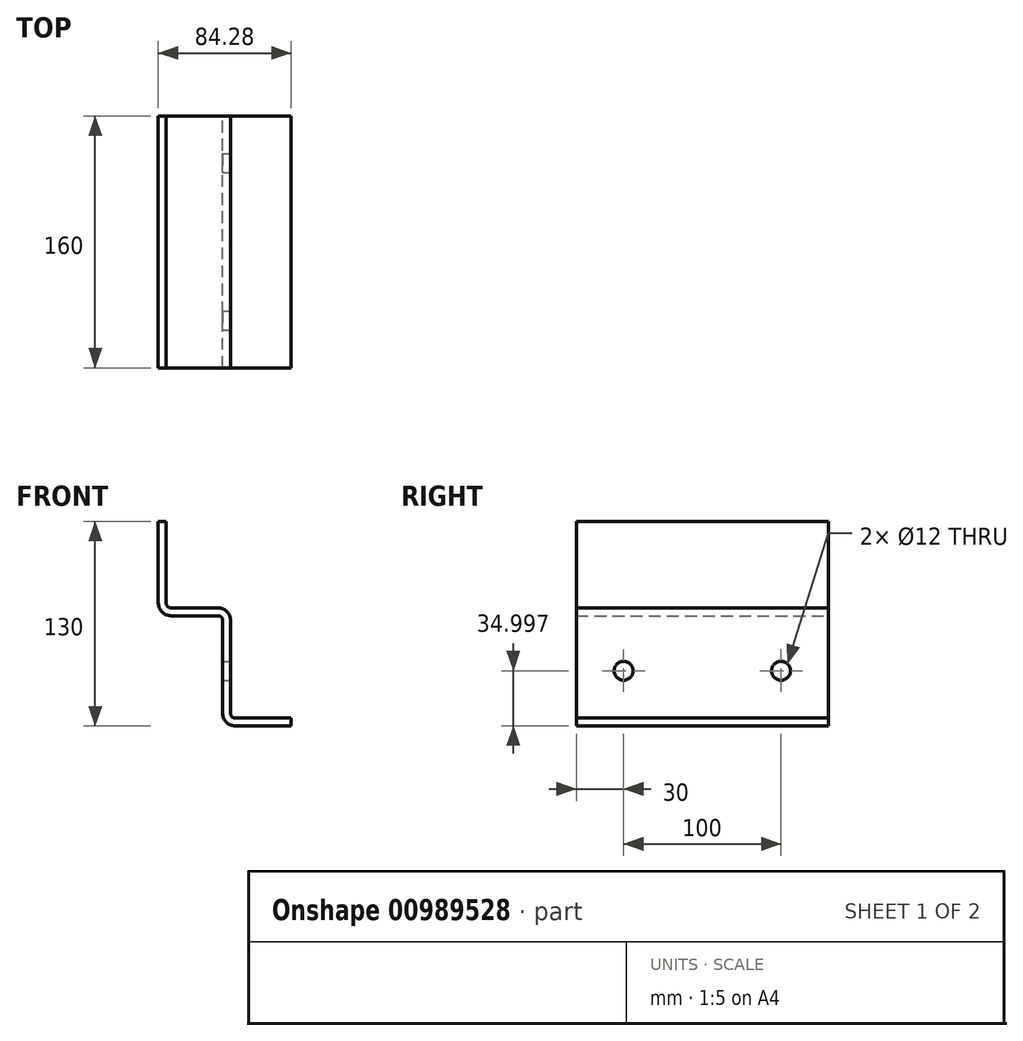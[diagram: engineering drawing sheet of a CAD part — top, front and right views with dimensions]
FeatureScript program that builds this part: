
annotation { "Feature Type Name" : "Feature", "Feature Type Description" : "" }
export const myFeature = defineFeature(function(context is Context, id is Id, definition is map)
    precondition{}
    {
        {
            var Q0;
            Q0=qCreatedBy(makeId("Front.planeOp"),FACE);
            var sketch = newSketch(context, id + "F0", { "sketchPlane" : qUnion([Q0])});
            skLineSegment(sketch, "E0", {"start": v(-40.9, 34.6) * mm, "end": v(-40.9, -17.4) * mm});
            skLineSegment(sketch, "E1", {"start": v(-32.9, -25.4) * mm, "end": v(-3, -25.4) * mm});
            skLineSegment(sketch, "E2", {"start": v(0, -28.4) * mm, "end": v(0, -87.4) * mm});
            skLineSegment(sketch, "E3", {"start": v(8, -95.4) * mm, "end": v(43.4, -95.4) * mm});
            skLineSegment(sketch, "E4", {"start": v(43.4, -95.4) * mm, "end": v(43.4, -90.4) * mm});
            skLineSegment(sketch, "E5", {"start": v(43.4, -90.4) * mm, "end": v(8, -90.4) * mm});
            skLineSegment(sketch, "E6", {"start": v(5, -87.4) * mm, "end": v(5, -28.4) * mm});
            skLineSegment(sketch, "E7", {"start": v(-3, -20.4) * mm, "end": v(-32.9, -20.4) * mm});
            skLineSegment(sketch, "E8", {"start": v(-35.9, -17.4) * mm, "end": v(-35.9, 34.6) * mm});
            skLineSegment(sketch, "E9", {"start": v(-35.9, 34.6) * mm, "end": v(-40.9, 34.6) * mm});
            skArc(sketch, "E10.filletArc", {"start": v(-35.9, -17.4) * mm, "mid": v(-35.01, -19.51) * mm, "end": v(-32.9, -20.4) * mm});
            skPoint(sketch, "E11.visualSharp", {"position": v(0, -25.4) * mm});
            skArc(sketch, "E11.filletArc", {"start": v(0, -28.4) * mm, "mid": v(-0.88, -26.27) * mm, "end": v(-3, -25.4) * mm});
            skPoint(sketch, "E12.visualSharp", {"position": v(5, -90.4) * mm});
            skArc(sketch, "E12.filletArc", {"start": v(5, -87.4) * mm, "mid": v(5.88, -89.51) * mm, "end": v(8, -90.4) * mm});
            skPoint(sketch, "E13.visualSharp", {"position": v(-40.9, -25.4) * mm});
            skArc(sketch, "E13.filletArc", {"start": v(-40.9, -17.4) * mm, "mid": v(-38.55, -23.05) * mm, "end": v(-32.9, -25.4) * mm});
            skPoint(sketch, "E14.visualSharp", {"position": v(0, -95.4) * mm});
            skArc(sketch, "E14.filletArc", {"start": v(0, -87.4) * mm, "mid": v(2.34, -93.05) * mm, "end": v(8, -95.4) * mm});
            skPoint(sketch, "E15.visualSharp", {"position": v(5, -20.4) * mm});
            skArc(sketch, "E15.filletArc", {"start": v(5, -28.4) * mm, "mid": v(2.66, -22.74) * mm, "end": v(-3, -20.4) * mm});
            skSolve(sketch);
        }
        {
            var Q0;
            Q0=makeQuery(id+"F0.imprint","IMPRINT",FACE,{"disambiguationData":[TD([[makeQuery(id+"F0.imprint","IMPRINT",EDGE,{"derivedFrom":sQuery(id+"F0.wireOp",EDGE,"E0")}),1.0]])]});
            extrude(context, id + "F1", {"entities" : qUnion([Q0]), "depth" : 160 * mm, "offsetDistance" : 25 * mm});
        }
        {
            var Q0;
            Q0=makeQuery(id+"F1.opExtrude","SWEPT_FACE",FACE,{"disambiguationData":[OSD([sQuery(id+"F0.wireOp",EDGE,"E2")])]});
            var sketch = newSketch(context, id + "F2", { "sketchPlane" : qUnion([Q0])});
            skPoint(sketch, "E16", {"position": v(0, -57.9) * mm});
            skPoint(sketch, "E17", {"position": v(30, -60.4) * mm});
            skPoint(sketch, "E18", {"position": v(130, -60.4) * mm});
            skSolve(sketch);
        }
        {
            var Q0;
            Q0=sQuery(id+"F2.wireOp",VERTEX,"E17");
            var Q1;
            Q1=sQuery(id+"F2.wireOp",VERTEX,"E18");
            var Q2;
            Q2=makeQuery(id+"F1.opExtrude","SWEPT_BODY",BODY,{"disambiguationData":[OSD([sQuery(id+"F0.wireOp",EDGE,"E0"),sQuery(id+"F0.wireOp",EDGE,"E1"),sQuery(id+"F0.wireOp",EDGE,"E2"),sQuery(id+"F0.wireOp",EDGE,"E3"),sQuery(id+"F0.wireOp",EDGE,"E4"),sQuery(id+"F0.wireOp",EDGE,"E5"),sQuery(id+"F0.wireOp",EDGE,"E6"),sQuery(id+"F0.wireOp",EDGE,"E7"),sQuery(id+"F0.wireOp",EDGE,"E8"),sQuery(id+"F0.wireOp",EDGE,"E9"),sQuery(id+"F0.wireOp",EDGE,"E10.filletArc"),sQuery(id+"F0.wireOp",EDGE,"E11.filletArc"),sQuery(id+"F0.wireOp",EDGE,"E12.filletArc"),sQuery(id+"F0.wireOp",EDGE,"E13.filletArc"),sQuery(id+"F0.wireOp",EDGE,"E14.filletArc"),sQuery(id+"F0.wireOp",EDGE,"E15.filletArc")])]});
            hole(context, id + "F3", {"style" : HoleStyle.SIMPLE, "endStyle" : HoleEndStyle.THROUGH, "holeDiameter" : 12 * mm, "majorDiameter" : 5 * mm, "isTappedThrough" : true, "tappedDepth" : 12 * mm, "tapClearance" : 3, "locations" : qUnion([Q0, Q1]), "scope" : qUnion([Q2])});
        }
    });
